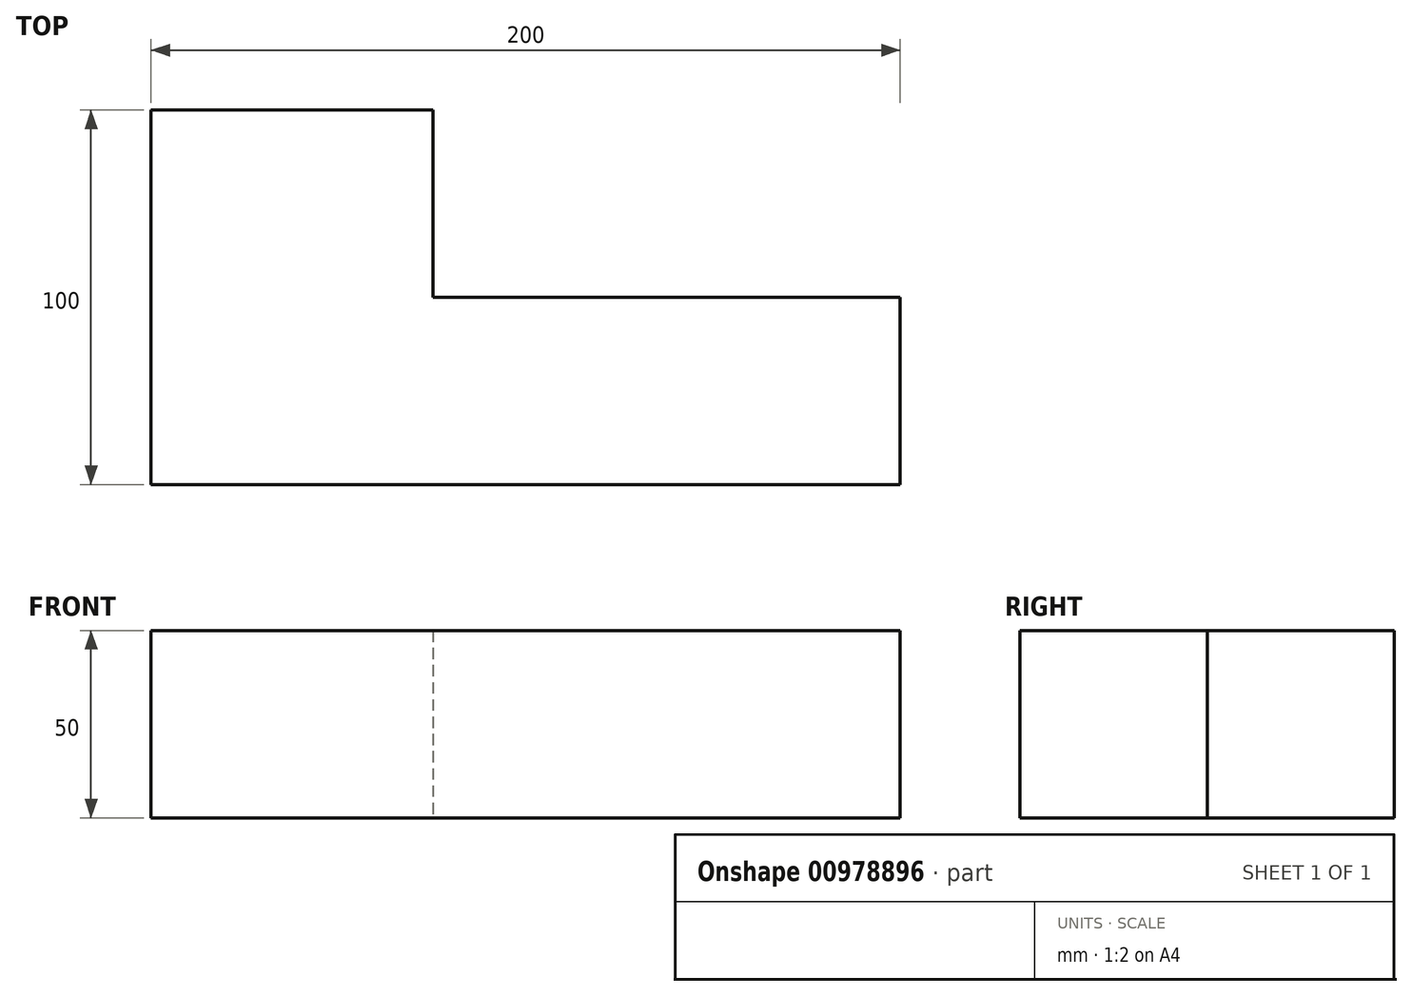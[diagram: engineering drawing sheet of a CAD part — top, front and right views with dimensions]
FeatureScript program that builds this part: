
annotation { "Feature Type Name" : "Feature", "Feature Type Description" : "" }
export const myFeature = defineFeature(function(context is Context, id is Id, definition is map)
    precondition{}
    {
        {
            var Q0;
            Q0=qCreatedBy(makeId("Top.planeOp"),FACE);
            var sketch = newSketch(context, id + "F0", { "sketchPlane" : qUnion([Q0])});
            skLineSegment(sketch, "E0", {"start": v(-75.26, 50) * mm, "end": v(-75.26, -50) * mm});
            skLineSegment(sketch, "E1", {"start": v(-75.26, -50) * mm, "end": v(124.74, -50) * mm});
            skLineSegment(sketch, "E2", {"start": v(124.74, -50) * mm, "end": v(124.74, 0) * mm});
            skLineSegment(sketch, "E3", {"start": v(124.74, 0) * mm, "end": v(0, 0) * mm});
            skLineSegment(sketch, "E4", {"start": v(0, 0) * mm, "end": v(0, 50) * mm});
            skLineSegment(sketch, "E5", {"start": v(0, 50) * mm, "end": v(-75.26, 50) * mm});
            skSolve(sketch);
        }
        {
            var Q0;
            Q0=makeQuery(id+"F0.imprint","IMPRINT",FACE,{"disambiguationData":[TD([[makeQuery(id+"F0.imprint","IMPRINT",EDGE,{"derivedFrom":sQuery(id+"F0.wireOp",EDGE,"E0")}),1.0]])]});
            extrude(context, id + "F1", {"entities" : qUnion([Q0]), "depth" : 50 * mm, "offsetDistance" : 25 * mm});
        }
    });
